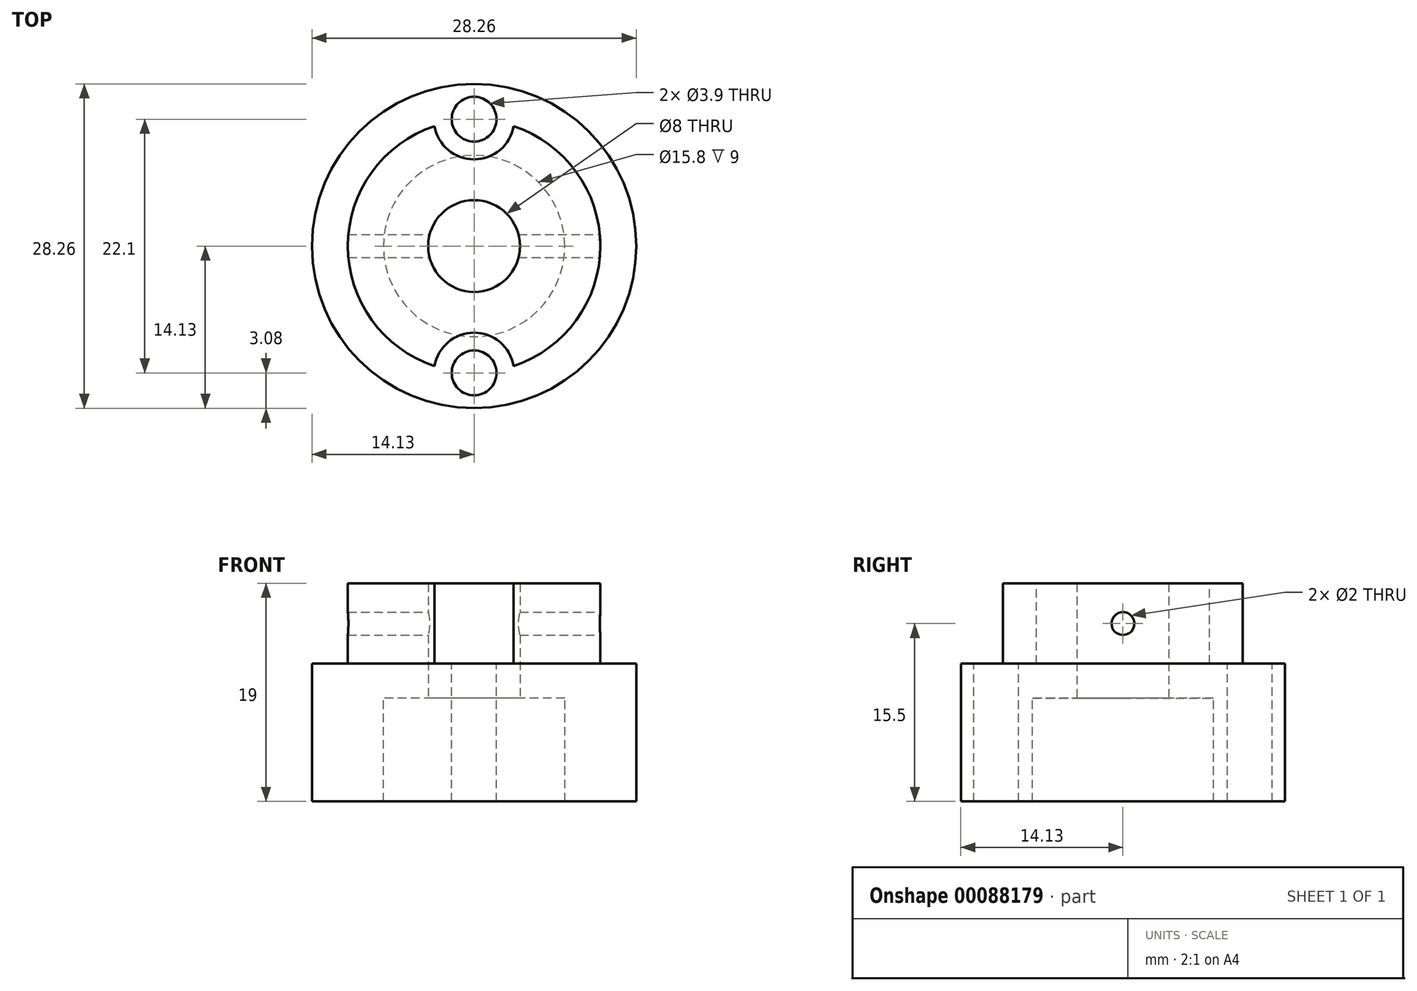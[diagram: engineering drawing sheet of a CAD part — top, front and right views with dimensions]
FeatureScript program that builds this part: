
annotation { "Feature Type Name" : "Feature", "Feature Type Description" : "" }
export const myFeature = defineFeature(function(context is Context, id is Id, definition is map)
    precondition{}
    {
        {
            var Q0;
            Q0=qCreatedBy(makeId("Top.planeOp"),FACE);
            var sketch = newSketch(context, id + "F0", { "sketchPlane" : qUnion([Q0])});
            skCircle(sketch, "E0", {"center": v(0, 0) * mm, "radius": 4 * mm});
            skCircle(sketch, "E1", {"center": v(0, 0) * mm, "radius": 14.12 * mm});
            skCircle(sketch, "E2", {"center": v(0, 0) * mm, "radius": 11 * mm});
            skSolve(sketch);
        }
        {
            var Q0;
            Q0=makeQuery(id+"F0.imprint","IMPRINT",FACE,{"disambiguationData":[TD([[makeQuery(id+"F0.imprint","IMPRINT",EDGE,{"derivedFrom":sQuery(id+"F0.wireOp",EDGE,"E1")}),1.0]])]});
            var Q1;
            Q1=makeQuery(id+"F0.imprint","IMPRINT",FACE,{"disambiguationData":[TD([[makeQuery(id+"F0.imprint","IMPRINT",EDGE,{"derivedFrom":sQuery(id+"F0.wireOp",EDGE,"E0")}),-1.0]])]});
            extrude(context, id + "F1", {"entities" : qUnion([Q0, Q1]), "depth" : 3 * mm});
        }
        {
            var Q0;
            Q0=makeQuery(id+"F0.imprint","IMPRINT",FACE,{"disambiguationData":[TD([[makeQuery(id+"F0.imprint","IMPRINT",EDGE,{"derivedFrom":sQuery(id+"F0.wireOp",EDGE,"E0")}),-1.0]])]});
            extrude(context, id + "F2", {"entities" : qUnion([Q0]), "operationType" : NewBodyOperationType.ADD, "depth" : 10 * mm});
        }
        {
            var Q0;
            Q0=qCreatedBy(makeId("Top.planeOp"),FACE);
            var sketch = newSketch(context, id + "F3", { "sketchPlane" : qUnion([Q0])});
            skCircle(sketch, "E3", {"center": v(0, 0) * mm, "radius": 7.9 * mm});
            skCircle(sketch, "E4", {"center": v(0, 0) * mm, "radius": 14.12 * mm});
            skSolve(sketch);
        }
        {
            var Q0;
            Q0=makeQuery(id+"F3.imprint","IMPRINT",FACE,{"disambiguationData":[TD([[makeQuery(id+"F3.imprint","IMPRINT",EDGE,{"derivedFrom":sQuery(id+"F3.wireOp",EDGE,"E3")}),-1.0]])]});
            extrude(context, id + "F4", {"entities" : qUnion([Q0]), "operationType" : NewBodyOperationType.ADD, "oppositeDirection" : true, "depth" : 9 * mm});
        }
        {
            var Q0;
            Q0=makeQuery(id+"F1.opExtrude","CAP_FACE",FACE,{"disambiguationData":[OSD([sQuery(id+"F0.wireOp",EDGE,"E0"),sQuery(id+"F0.wireOp",EDGE,"E1")])],"isStart":false});
            var sketch = newSketch(context, id + "F5", { "sketchPlane" : qUnion([Q0])});
            skCircle(sketch, "E5", {"center": v(0, 11.05) * mm, "radius": 1.95 * mm});
            skCircle(sketch, "E6", {"center": v(0, -11.05) * mm, "radius": 1.95 * mm});
            skSolve(sketch);
        }
        {
            var Q0;
            Q0=makeQuery(id+"F5.imprint","IMPRINT",FACE,{"disambiguationData":[TD([[makeQuery(id+"F5.imprint","IMPRINT",EDGE,{"derivedFrom":sQuery(id+"F5.wireOp",EDGE,"E5")}),1.0]])]});
            var Q1;
            Q1=makeQuery(id+"F5.imprint","IMPRINT",FACE,{"disambiguationData":[TD([[makeQuery(id+"F5.imprint","IMPRINT",EDGE,{"derivedFrom":sQuery(id+"F5.wireOp",EDGE,"E6")}),1.0]])]});
            var Q2;
            Q2=makeQuery(id+"F4.opExtrude","CAP_FACE",FACE,{"disambiguationData":[OSD([sQuery(id+"F3.wireOp",EDGE,"E3"),sQuery(id+"F3.wireOp",EDGE,"E4")])],"isStart":false});
            extrude(context, id + "F6", {"entities" : qUnion([Q0, Q1]), "operationType" : NewBodyOperationType.REMOVE, "endBound" : BoundingType.UP_TO_SURFACE, "oppositeDirection" : true, "endBoundEntityFace" : qUnion([Q2]), "depth" : 25 * mm});
        }
        {
            var Q0;
            Q0=qCreatedBy(makeId("Right.planeOp"),FACE);
            var sketch = newSketch(context, id + "F7", { "sketchPlane" : qUnion([Q0])});
            skCircle(sketch, "E7", {"center": v(0, 6.5) * mm, "radius": 1 * mm});
            skSolve(sketch);
        }
        {
            var Q0;
            Q0=makeQuery(id+"F7.imprint","IMPRINT",FACE,{"disambiguationData":[TD([[makeQuery(id+"F7.imprint","IMPRINT",EDGE,{"derivedFrom":sQuery(id+"F7.wireOp",EDGE,"E7")}),1.0]])]});
            extrude(context, id + "F8", {"entities" : qUnion([Q0]), "operationType" : NewBodyOperationType.REMOVE, "endBound" : BoundingType.SYMMETRIC, "oppositeDirection" : true, "depth" : 25 * mm});
        }
        {
            var Q0;
            Q0=makeQuery(id+"F2.opExtrude","CAP_FACE",FACE,{"disambiguationData":[OSD([sQuery(id+"F0.wireOp",EDGE,"E0"),sQuery(id+"F0.wireOp",EDGE,"E2")])],"isStart":false});
            var sketch = newSketch(context, id + "F9", { "sketchPlane" : qUnion([Q0])});
            skCircle(sketch, "E8", {"center": v(0, 11.05) * mm, "radius": 3.5 * mm});
            skCircle(sketch, "E9", {"center": v(0, -11.05) * mm, "radius": 3.5 * mm});
            skSolve(sketch);
        }
        {
            var Q0;
            {var subQ0=sQuery(id+"F9.wireOp",EDGE,"E8");var subQ1=makeQuery(id+"F2.opExtrude","CAP_EDGE",EDGE,{"disambiguationData":[OSD([sQuery(id+"F0.wireOp",EDGE,"E2")])],"isStart":false});var subQ2=makeQuery(id+"F9.imprint","INTERSECT",VERTEX,{"disambiguationData":[OD(0.0)],"derivedFrom":[subQ1,subQ0]});Q0=makeQuery(id+"F9.imprint","IMPRINT",FACE,{"disambiguationData":[TD([[makeQuery(id+"F9.imprint","IMPRINT",EDGE,{"disambiguationData":[TD([[subQ2,-1.0]])],"derivedFrom":subQ0}),1.0]])]});}
            var Q1;
            {var subQ0=sQuery(id+"F9.wireOp",EDGE,"E9");var subQ1=makeQuery(id+"F2.opExtrude","CAP_EDGE",EDGE,{"disambiguationData":[OSD([sQuery(id+"F0.wireOp",EDGE,"E2")])],"isStart":false});var subQ2=makeQuery(id+"F9.imprint","INTERSECT",VERTEX,{"disambiguationData":[OD(0.0)],"derivedFrom":[subQ1,subQ0]});Q1=makeQuery(id+"F9.imprint","IMPRINT",FACE,{"disambiguationData":[TD([[makeQuery(id+"F9.imprint","IMPRINT",EDGE,{"disambiguationData":[TD([[subQ2,1.0]])],"derivedFrom":subQ0}),1.0]])]});}
            var Q2;
            Q2=makeQuery(id+"F1.opExtrude","CAP_FACE",FACE,{"disambiguationData":[OSD([sQuery(id+"F0.wireOp",EDGE,"E0"),sQuery(id+"F0.wireOp",EDGE,"E1")])],"isStart":false});
            extrude(context, id + "F10", {"entities" : qUnion([Q0, Q1]), "operationType" : NewBodyOperationType.REMOVE, "endBound" : BoundingType.UP_TO_SURFACE, "oppositeDirection" : true, "endBoundEntityFace" : qUnion([Q2]), "depth" : 8 * mm});
        }
    });
